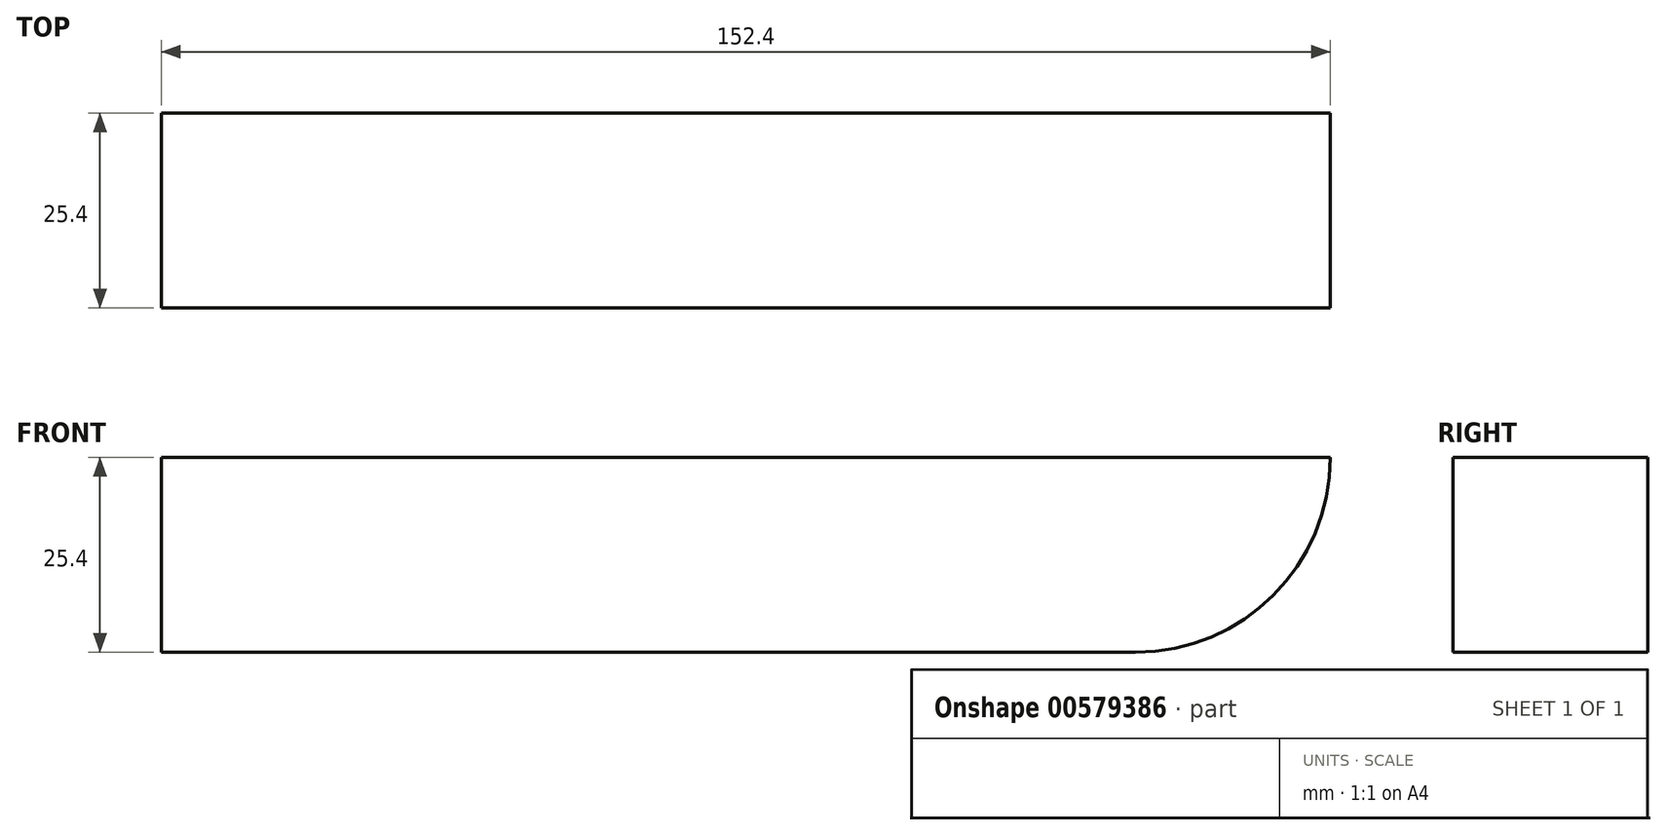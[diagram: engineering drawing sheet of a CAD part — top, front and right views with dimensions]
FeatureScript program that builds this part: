
annotation { "Feature Type Name" : "Feature", "Feature Type Description" : "" }
export const myFeature = defineFeature(function(context is Context, id is Id, definition is map)
    precondition{}
    {
        {
            var Q0;
            Q0=qCreatedBy(makeId("Front.planeOp"),FACE);
            var sketch = newSketch(context, id + "F0", { "sketchPlane" : qUnion([Q0])});
            skLineSegment(sketch, "E0.bottom", {"start": v(-78.47, 12.66) * mm, "end": v(48.53, 12.66) * mm});
            skLineSegment(sketch, "E0.top", {"start": v(-78.47, -12.74) * mm, "end": v(48.53, -12.74) * mm});
            skLineSegment(sketch, "E0.left", {"start": v(-78.47, 12.66) * mm, "end": v(-78.47, -12.74) * mm});
            skLineSegment(sketch, "E0.right", {"start": v(48.53, 12.66) * mm, "end": v(48.53, -12.74) * mm});
            skLineSegment(sketch, "E1", {"start": v(48.53, 12.66) * mm, "end": v(73.93, 12.66) * mm});
            skArc(sketch, "E2", {"start": v(48.53, -12.74) * mm, "mid": v(66.5, -5.3) * mm, "end": v(73.93, 12.66) * mm});
            skSolve(sketch);
        }
        {
            var Q0;
            Q0=makeQuery(id+"F0.imprint","IMPRINT",FACE,{"disambiguationData":[TD([[makeQuery(id+"F0.imprint","IMPRINT",EDGE,{"derivedFrom":sQuery(id+"F0.wireOp",EDGE,"E0.right")}),1.0]])]});
            var Q1;
            Q1=makeQuery(id+"F0.imprint","IMPRINT",FACE,{"disambiguationData":[TD([[makeQuery(id+"F0.imprint","IMPRINT",EDGE,{"derivedFrom":sQuery(id+"F0.wireOp",EDGE,"E0.bottom")}),-1.0]])]});
            extrude(context, id + "F1", {"entities" : qUnion([Q0, Q1]), "depth" : 25.4 * mm, "offsetDistance" : 25.4 * mm});
        }
    });
